# Revit family: Sanitary_Shower-Trays_Sanindusa_Piano-Shower-Tray
name_source: partatom
category: Plumbing Fixtures
revit_build: Autodesk Revit 2018 (Build: 20170223_1515(x64)
units: mm (PartAtom-declared; Revit-internal decimal feet)

## family parameters
Always vertical = Yes
Cut with Voids When Loaded = No
OmniClass Number = 23.45.00.00
OmniClass Title = Sanitary, Laundry, and Cleaning Equipment
Part Type = Normal
Room Calculation Point = No
Round Connector Dimension = Use Diameter
Shared = No
Work Plane-Based = No

## types (1)
- Sanitary_Shower-Trays_Sanindusa_Piano-Shower-Tray
    AssetType = Fixed
    CodePerformance = EN 14527:2006 / A1:2010
CL 2
    Color = white
    Constituents = 49911-90 shower tray drain (not included)
    Cost = 0 $
    Description = smooth surface shower tray
    DrainSize = 90 mm  [stored 0.295276 ft]
    Edition number = 1
    Element Type = SHOWER: Installation or waste water appliance that emits a spray of water to wash the human body (BS6100)
    Features = Domestic and commercial use. Built-in shower tray. Contemporary design. Range with various sizes and depths available.
    Finish = gloss
    Installation Instructions = https://www.tec.sanindusa.pt
    InstallationDate = 1900-12-31T23:59:59
    Manufacturer = Sanindusa
    ManufacturerName = Sanindusa
    ManufacturerURL = www.tec.sanindusa.pt
    Material = Acrylic
    ModelNumber = 8035200000
    ModelReference = Piano
    Name = 80X80x3.5 piano shower tray
    NominalHeight = 68 mm
    NominalLength = 800 mm  [stored 2.62467 ft]
    NominalWidth = 800 mm  [stored 2.62467 ft]
    Pre-defined type (IFC) = SHOWER
    Product Guid = 73abca29-ca93-49ce-8f49-db031d0bdf09
    Product data url = https://bimobject.com
    ProductInformation = https://www.tec.sanindusa.pt
    ProductionYear = 2018
    Shape = square
    Size = 80x80
    Type (IFC) = IfcSanitaryTerminalType
    URL = www.tec.sanindusa.pt
    Uniclass2015Code = Pr_40_20_06_84
    Uniclass2015Title = Shower trays
    Uniclass2015Version = Products v1.6
    Version = 1
    WarrantyDescription = https://www.tec.sanindusa.pt
    WarrantyDurationParts = 5
    WarrantyDurationUnit = year
    WarrantyStartDate = 1900-12-31T23:59:59
1900-12-31T23:59:59
    Weight = 11.00 kg

note: [stored X ft] marks values corroborated as IEEE doubles in the binary element streams (Revit-internal decimal feet)

## geometry (parser evidence)
native form markers: Sweep x8
no freeform markers — native parametric forms only
